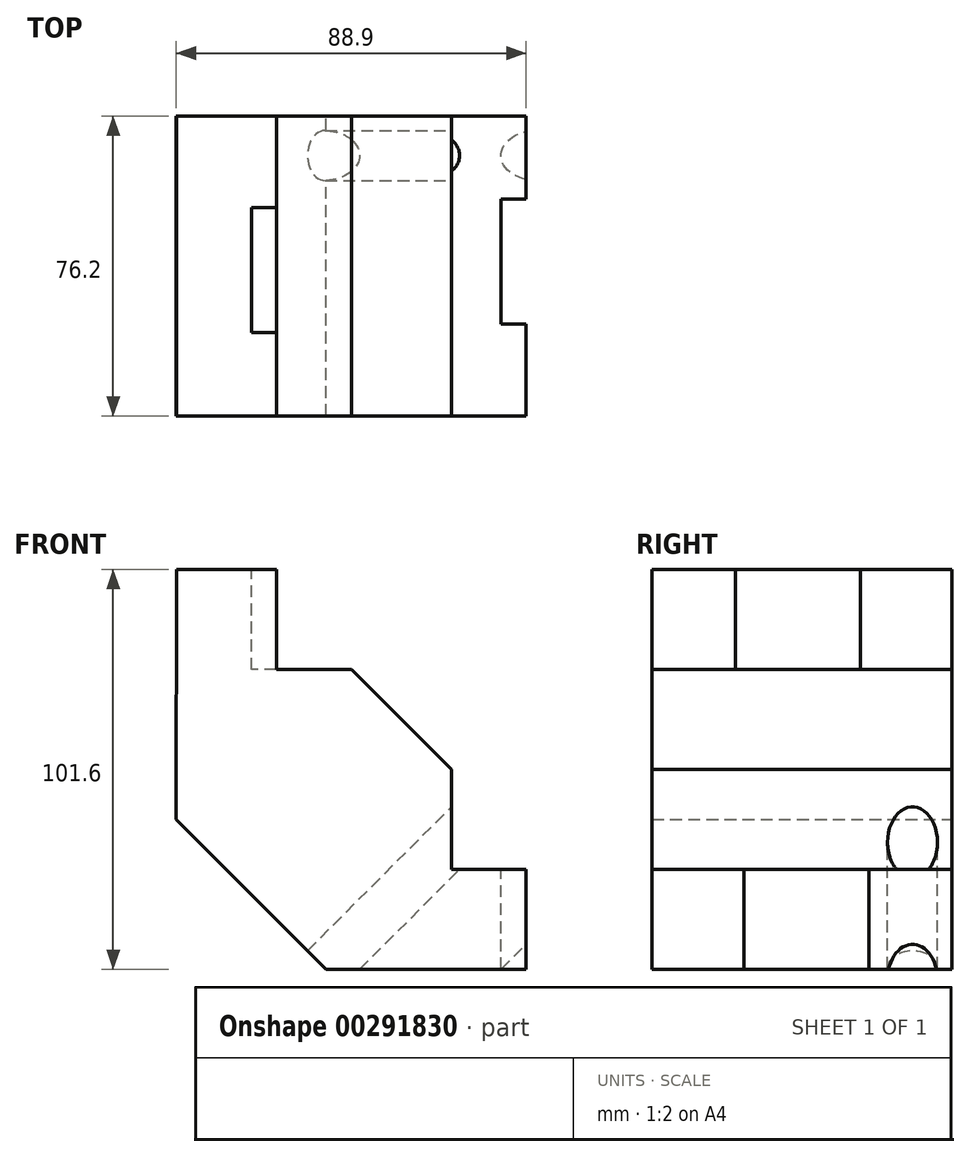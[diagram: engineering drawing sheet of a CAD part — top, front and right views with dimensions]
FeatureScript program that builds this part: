
annotation { "Feature Type Name" : "Feature", "Feature Type Description" : "" }
export const myFeature = defineFeature(function(context is Context, id is Id, definition is map)
    precondition{}
    {
        {
            var Q0;
            Q0=qCreatedBy(makeId("Front.planeOp"),FACE);
            var sketch = newSketch(context, id + "F0", { "sketchPlane" : qUnion([Q0])});
            skLineSegment(sketch, "E0", {"start": v(27.8, -53.2) * mm, "end": v(27.8, -27.8) * mm});
            skLineSegment(sketch, "E1", {"start": v(27.8, -27.8) * mm, "end": v(8.82, -27.8) * mm});
            skLineSegment(sketch, "E2", {"start": v(8.82, -27.8) * mm, "end": v(8.82, -2.4) * mm});
            skLineSegment(sketch, "E3", {"start": v(-61.03, 48.4) * mm, "end": v(-35.63, 48.38) * mm});
            skLineSegment(sketch, "E4", {"start": v(-35.63, 48.38) * mm, "end": v(-35.66, 23.03) * mm});
            skLineSegment(sketch, "E5", {"start": v(-35.66, 23.03) * mm, "end": v(-16.58, 23) * mm});
            skLineSegment(sketch, "E6", {"start": v(-16.58, 23) * mm, "end": v(8.82, -2.4) * mm});
            skLineSegment(sketch, "E7", {"start": v(-61.03, 48.4) * mm, "end": v(-61.1, -15.1) * mm});
            skLineSegment(sketch, "E8", {"start": v(27.8, -53.2) * mm, "end": v(-23, -53.2) * mm});
            skLineSegment(sketch, "E9", {"start": v(-61.1, -15.1) * mm, "end": v(-23, -53.2) * mm});
            skSolve(sketch);
        }
        {
            var Q0;
            Q0 = qSketchRegion(id + "F0", true);
            var Q1;
            Q1=sQuery(id+"F0.wireOp",EDGE,"E7");
            var Q2;
            Q2=sQuery(id+"F0.wireOp",EDGE,"E9");
            var Q3;
            Q3=sQuery(id+"F0.wireOp",EDGE,"E5");
            var Q4;
            Q4=sQuery(id+"F0.wireOp",EDGE,"E1");
            var Q5;
            Q5=sQuery(id+"F0.wireOp",EDGE,"E6");
            var Q6;
            Q6=sQuery(id+"F0.wireOp",EDGE,"7bO9rM5X-PQ9u-uV3v-F5ej-F69AUwboWV7c");
            var Q7;
            Q7=sQuery(id+"F0.wireOp",EDGE,"vmyMyaEW-hDar-hYg1-nAbB-GNXIQ0UiH5dv");
            var Q8;
            Q8=sQuery(id+"F0.wireOp",EDGE,"E2");
            var Q9;
            Q9=sQuery(id+"F0.wireOp",EDGE,"E4");
            var Q10;
            Q10=sQuery(id+"F0.wireOp",EDGE,"E3");
            var Q11;
            Q11=sQuery(id+"F0.wireOp",EDGE,"E0");
            var Q12;
            Q12=sQuery(id+"F0.wireOp",EDGE,"E8");
            extrude(context, id + "F1", {"entities" : qUnion([Q0]), "surfaceEntities" : qUnion([Q1, Q2, Q3, Q4, Q5, Q6, Q7, Q8, Q9, Q10, Q11, Q12]), "depth" : 76.2 * mm});
        }
        {
            var Q0;
            Q0=makeQuery(id+"F1.opExtrude","SWEPT_FACE",FACE,{"disambiguationData":[OSD([sQuery(id+"F0.wireOp",EDGE,"E6")])]});
            var sketch = newSketch(context, id + "F2", { "sketchPlane" : qUnion([Q0])});
            skPoint(sketch, "E10.centerSnap0", {"position": v(-10.03, 0) * mm});
            skCircle(sketch, "E11", {"center": v(-10.03, -59.1) * mm, "radius": 6.35 * mm});
            skCircle(sketch, "E12", {"center": v(-10.03, -21) * mm, "radius": 6.35 * mm});
            skSolve(sketch);
        }
        {
            var Q0;
            Q0=makeQuery(id+"F1.opExtrude","SWEPT_FACE",FACE,{"disambiguationData":[OSD([sQuery(id+"F0.wireOp",EDGE,"E3")])]});
            var sketch = newSketch(context, id + "F3", { "sketchPlane" : qUnion([Q0])});
            skLineSegment(sketch, "E13", {"start": v(-61.09, -76.2) * mm, "end": v(-61.09, 0) * mm});
            skLineSegment(sketch, "E14", {"start": v(-35.69, -23.27) * mm, "end": v(-42.04, -23.27) * mm});
            skLineSegment(sketch, "E15", {"start": v(-42.04, -23.27) * mm, "end": v(-42.04, -55.02) * mm});
            skLineSegment(sketch, "E16", {"start": v(-42.04, -55.02) * mm, "end": v(-35.69, -55.02) * mm});
            skLineSegment(sketch, "E17", {"start": v(-61.09, 0) * mm, "end": v(-35.69, 0) * mm});
            skLineSegment(sketch, "E18", {"start": v(-35.69, 0) * mm, "end": v(-35.69, -23.27) * mm});
            skLineSegment(sketch, "E19", {"start": v(-35.69, -55.02) * mm, "end": v(-35.69, -76.2) * mm});
            skLineSegment(sketch, "E20", {"start": v(-61.09, -76.2) * mm, "end": v(-35.69, -76.2) * mm});
            skLineSegment(sketch, "E21", {"start": v(-35.69, -23.27) * mm, "end": v(-35.69, -55.02) * mm});
            skSolve(sketch);
        }
        {
            var Q0;
            Q0 = qSketchRegion(id + "F2", true);
            extrude(context, id + "F4", {"entities" : qUnion([Q0]), "operationType" : NewBodyOperationType.REMOVE, "oppositeDirection" : true, "offsetDistance" : 25.4 * mm, "depth" : 58.42 * mm});
        }
        {
            var Q0;
            Q0=makeQuery(id+"F1.opExtrude","SWEPT_FACE",FACE,{"disambiguationData":[OSD([sQuery(id+"F0.wireOp",EDGE,"E1")])]});
            var sketch = newSketch(context, id + "F5", { "sketchPlane" : qUnion([Q0])});
            skLineSegment(sketch, "E22", {"start": v(27.8, -21.13) * mm, "end": v(21.45, -21.13) * mm});
            skLineSegment(sketch, "E23", {"start": v(21.45, -21.13) * mm, "end": v(21.45, -52.88) * mm});
            skLineSegment(sketch, "E24", {"start": v(21.45, -52.88) * mm, "end": v(27.8, -52.88) * mm});
            skLineSegment(sketch, "E25", {"start": v(27.8, -21.13) * mm, "end": v(27.8, -52.88) * mm});
            skSolve(sketch);
        }
        {
            var Q0;
            Q0=makeQuery(id+"F5.imprint","IMPRINT",FACE,{"disambiguationData":[TD([[makeQuery(id+"F5.imprint","IMPRINT",EDGE,{"derivedFrom":sQuery(id+"F5.wireOp",EDGE,"E22")}),1.0]])]});
            var Q1;
            Q1=sQuery(id+"F5.wireOp",EDGE,"E22");
            var Q2;
            Q2=sQuery(id+"F5.wireOp",EDGE,"E24");
            var Q3;
            Q3=sQuery(id+"F5.wireOp",EDGE,"E23");
            var Q4;
            Q4=sQuery(id+"F5.wireOp",EDGE,"E25");
            extrude(context, id + "F6", {"entities" : qUnion([Q0]), "operationType" : NewBodyOperationType.REMOVE, "surfaceEntities" : qUnion([Q1, Q2, Q3, Q4]), "oppositeDirection" : true, "offsetDistance" : 25.4 * mm, "depth" : 25.4 * mm});
        }
        {
            var Q0;
            Q0=makeQuery(id+"F3.imprint","IMPRINT",FACE,{"disambiguationData":[TD([[makeQuery(id+"F3.imprint","IMPRINT",EDGE,{"derivedFrom":sQuery(id+"F3.wireOp",EDGE,"E14")}),1.0]])]});
            extrude(context, id + "F7", {"entities" : qUnion([Q0]), "operationType" : NewBodyOperationType.REMOVE, "oppositeDirection" : true, "depth" : 25.4 * mm, "offsetDistance" : 25.4 * mm});
        }
    });
